# Revit family: SNS Merlin 1000VW+ Gas Pressure Proving
name_source: partatom
category: Electrical Equipment
units: mm (PartAtom-declared; Revit-internal decimal feet)

## family parameters
Always vertical = Yes
Cut with Voids When Loaded = No
OmniClass Number = 23.80.30.11.17
OmniClass Title = Distribution Boards and Control Panels
Part Type = Other Panel
Room Calculation Point = No
Round Connector Dimension = Use Diameter
Shared = No
Work Plane-Based = No

## types (1)
- AGS Merlin 1000VW+
    Default Height = 4' - 0"
    Description = The Merlin 1000VW+ Educational Laboratory Utility Controls allows the teacher to command the utilities available to the classroom at any given time whilst also including built in safety features to protect the classroom, students and the building. The Merlin 1000VW+ controls Water, Gas and Electricity with individual switches and time out functions. The gas pressure is tested using a unique digital transducer ensuring no open gas taps and no gas leaks. In built connectivity allows for connection to existing fire alarm and building management systems and with its easy to use system status panel and labeled PCB the Merlin 1000VW+ is easy to install and easy to operate.
    Load = 120 VA
    Manufacturer = S&S Northern Ltd.
    Model = SNS Merlin 1000VW+
    Product Information = https://snsnorthern.com
    Type Comments = Merlin 1000VW+ incl. Gas Pressure Proving Transducer protection.
    URL = https://snsnorthern.com
    Voltage = 120VAC

## geometry (parser evidence)
native form markers: Sweep x15
no freeform markers — native parametric forms only
